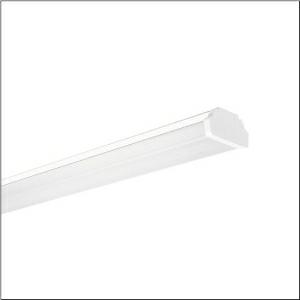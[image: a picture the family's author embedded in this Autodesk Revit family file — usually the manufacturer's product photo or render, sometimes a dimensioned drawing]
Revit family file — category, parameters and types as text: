
# Revit family: dus_31_gen_2_53bd812cv675c2_3805
name_source: partatom
category: Lighting Fixtures
units: mm (PartAtom-declared; Revit-internal decimal feet)

## family parameters
Cut with Voids When Loaded = No
Host = Face
Light Source = No
Part Type = Normal
Room Calculation Point = No
Round Connector Dimension = Use Diameter
Shared = No

## types (1)
- --- (1 x LED, 7670 lm, 42.1 W, 6500K)
    Apparent Load = 42 VA
    CIE Flux Codes = 47 80 95 93 100
    Color Rendering = 80
    Color Temperature = 6500K
    Default Elevation = 1800 mm
    Description = DUS 31 Gen.2, luminaire insert, of sheet steel, coil coated, white, length: 1.535mm, width: 81mm, height: 90mm, 5x system unit, system units: 307mm, LED rated luminous flux: 7.670lm, light colour: 865, SDCM (Standard Deviation of Colour Matching)MacAdam ≤ 3 SDCM (initial), control gear: ON/OFF Multilumen, CLOi, with plug, 3-pole, with phase selection, mains connection: 220..240V, AC, 50/60Hz, start of lifetime: 42W, end of service life: 50W, through-wiring accessed according to module size, primary optical cover: cover, of PMMA, light emission: direct distribution, primary light characteristic: symmetric, protection rating (complete): IP20, protection rating (LED compartment): IP50, insulation class (complete): insulation class I (protective earthing), certification: CE, ENEC, VDE, UKCA, impact resistance: IK03, permissible ambient temperature for indoor applications: -35..+50°C, corresponds to IFS (International Featured Standards) requirements for safety and quality in the food industry, reducing of maximum allowable ambient temperature of 5°C with ceiling mounting, packaging unit: 1 piece
    Height = 95 mm
    Lamp = 1 x LED
    Lamp Light Flux = 7670 lm
    Lamp Power = 42.1 W
    Lamp count = 1
    Length = 1535 mm
    Luminous efficacy = 182 lm/W
    Manufacturer = Siteco
    ModVariant = No
    Model = 53BD812CV675C2
    Mounting Place = Ceiling
    Mounting Type = Pendant
    Number of Poles = 1
    OnlyDefault = Yes
    Power Factor = 1
    Product Name = DUS 31 Gen.2
    Product group = luminaire insert | ceiling pendant
    ProductGroupID = 901
    Protection Class = Protection class I
    Protection Degree = IP 20
    RLX_Detail_Level = 1
    RLX_Emergency_Light_Flux = 0 lm
    RLX_Emergency_Type = 0
    RLX_Emergency_Type_DB = No
    RlxData = <blob elided: 29801 chars, md5=f5248292>
    Socket = socket
    Standby Power = 0 W
    System Light Flux = 7670 lm
    System Power = 42 W
    Type Comments = factory setting: luminous flux: 100 % | (A | C | E) | 98 mA
    Type Image = l_1319596.jpg
    URL = http://relux.com
    VarID = @adj_040803
    Voltage = 0 V
    Weight = 0.00 kg
    Width = 81 mm

## geometry (parser evidence)
native form markers: Blend x4, Sweep x12
no freeform markers — native parametric forms only
